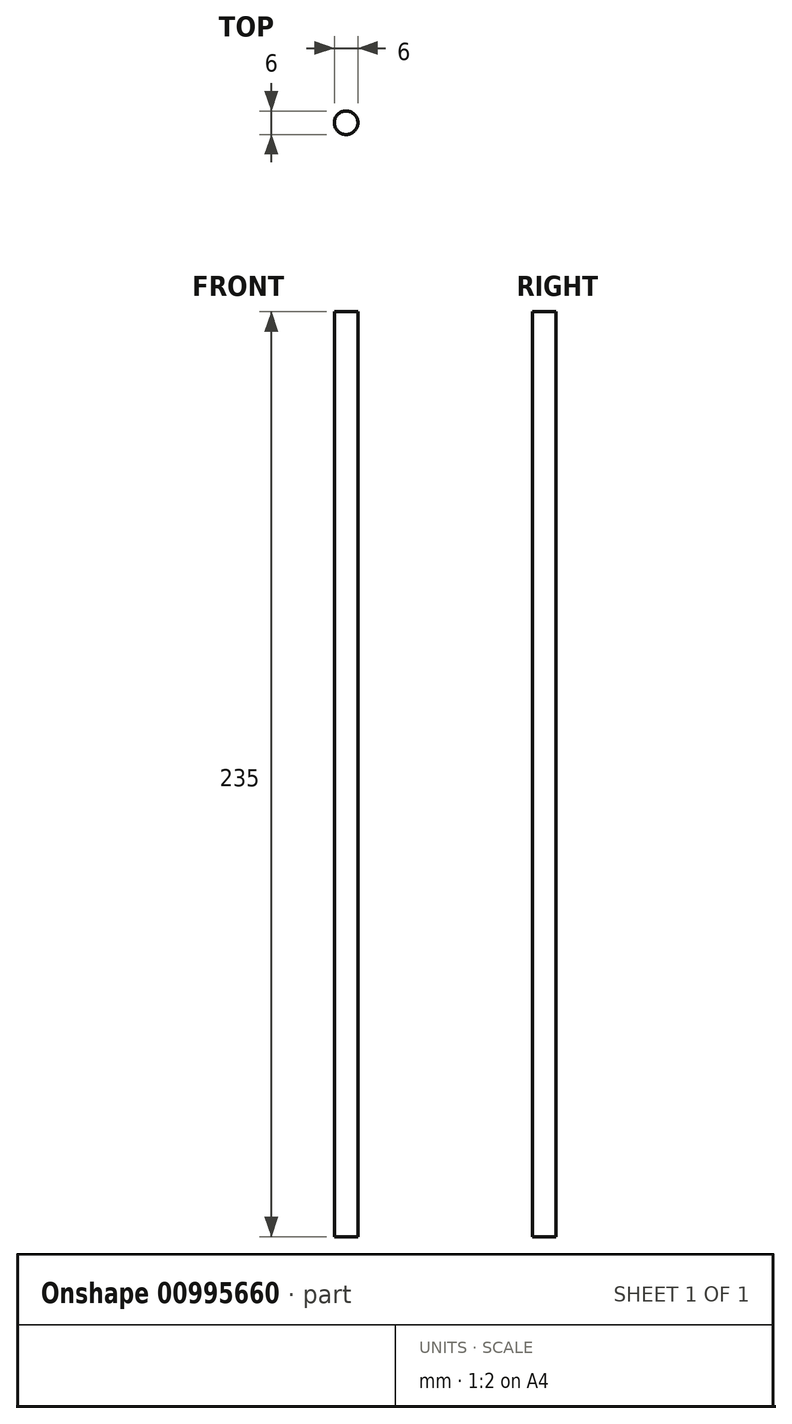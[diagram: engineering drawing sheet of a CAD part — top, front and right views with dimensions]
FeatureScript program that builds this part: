
annotation { "Feature Type Name" : "Feature", "Feature Type Description" : "" }
export const myFeature = defineFeature(function(context is Context, id is Id, definition is map)
    precondition{}
    {
        {
            var Q0;
            Q0=qCreatedBy(makeId("Top.planeOp"),FACE);
            var sketch = newSketch(context, id + "F0", { "sketchPlane" : qUnion([Q0]), "disableImprinting" : false});
            skCircle(sketch, "E0", {"center": v(0, 0) * mm, "radius": 3 * mm});
            skSolve(sketch);
        }
        {
            var Q0;
            Q0 = qSketchRegion(id + "F0", true);
            extrude(context, id + "F1", {"entities" : qUnion([Q0]), "depth" : 235 * mm, "offsetDistance" : 25 * mm, "symmetric" : true});
        }
    });
